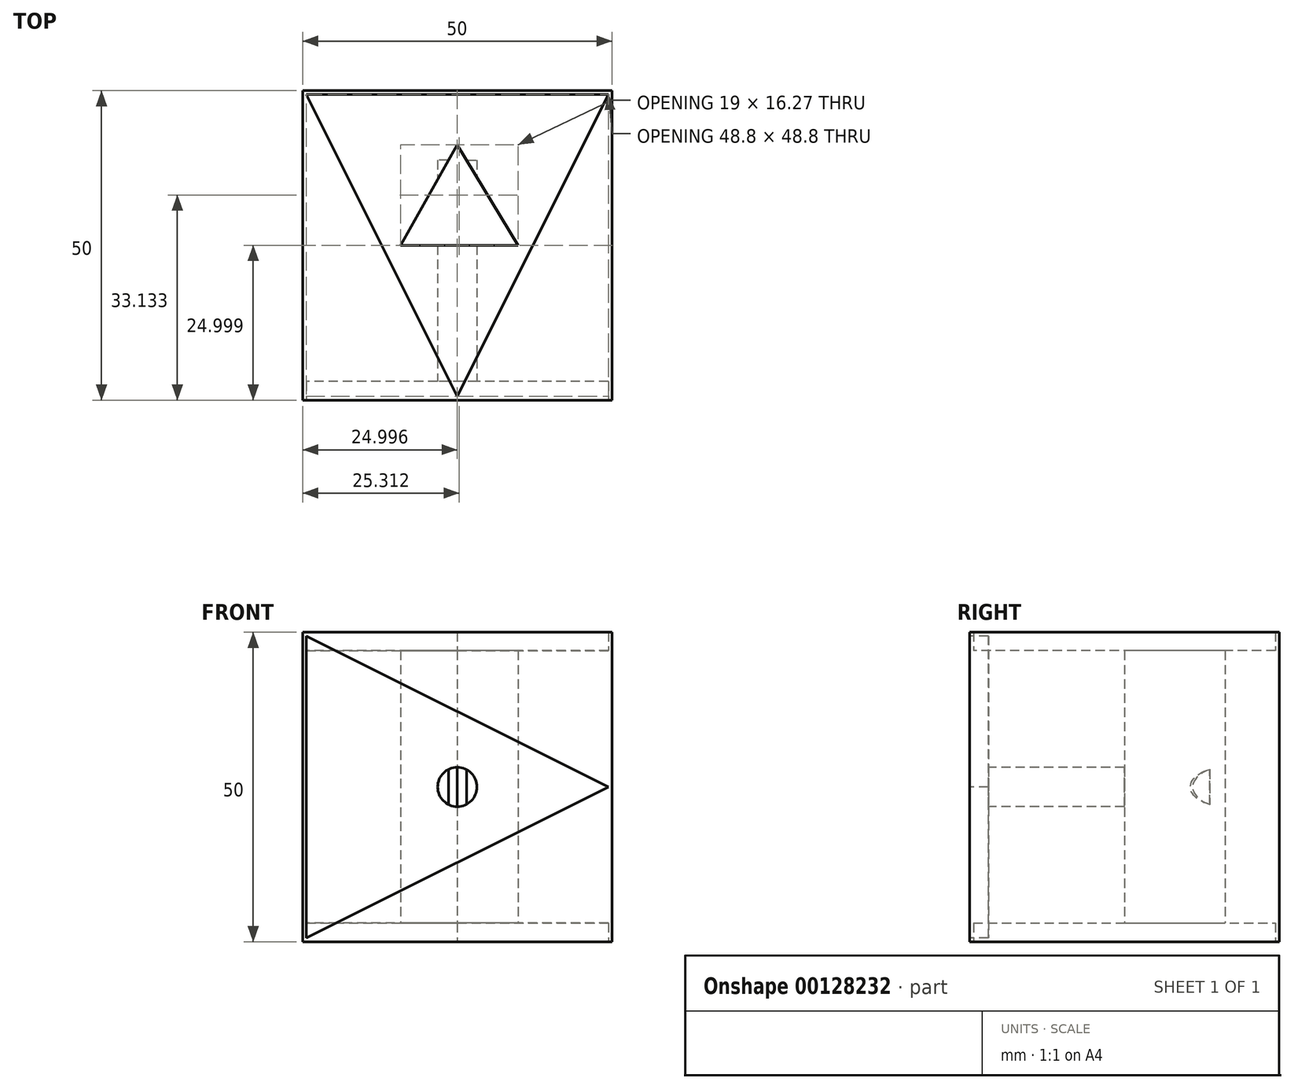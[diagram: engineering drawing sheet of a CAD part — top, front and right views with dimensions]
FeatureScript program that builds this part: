
annotation { "Feature Type Name" : "Feature", "Feature Type Description" : "" }
export const myFeature = defineFeature(function(context is Context, id is Id, definition is map)
    precondition{}
    {
        {
            var Q0;
            Q0=qCreatedBy(makeId("Top.planeOp"),FACE);
            var sketch = newSketch(context, id + "F0", { "sketchPlane" : qUnion([Q0])});
            skLineSegment(sketch, "E0", {"start": v(29.85, -17.75) * mm, "end": v(29.85, 32.25) * mm});
            skLineSegment(sketch, "E1", {"start": v(29.85, 32.25) * mm, "end": v(-20.15, 32.25) * mm});
            skLineSegment(sketch, "E2", {"start": v(-20.15, 32.25) * mm, "end": v(-20.15, -17.75) * mm});
            skLineSegment(sketch, "E3", {"start": v(29.85, -17.75) * mm, "end": v(-20.15, -17.75) * mm});
            skLineSegment(sketch, "E4", {"start": v(-19.56, 31.65) * mm, "end": v(4.85, -17.15) * mm});
            skLineSegment(sketch, "E5", {"start": v(4.85, -17.15) * mm, "end": v(29.25, 31.65) * mm});
            skLineSegment(sketch, "E6", {"start": v(29.25, 31.65) * mm, "end": v(-19.56, 31.65) * mm});
            skSolve(sketch);
        }
        {
            var Q0;
            Q0=makeQuery(id+"F0.imprint","IMPRINT",FACE,{"disambiguationData":[TD([[makeQuery(id+"F0.imprint","IMPRINT",EDGE,{"derivedFrom":sQuery(id+"F0.wireOp",EDGE,"E0")}),1.0]])]});
            extrude(context, id + "F1", {"entities" : qUnion([Q0]), "endBound" : BoundingType.SYMMETRIC, "depth" : 50 * mm});
        }
        {
            var Q0;
            Q0=makeQuery(id+"F0.imprint","IMPRINT",FACE,{"disambiguationData":[TD([[makeQuery(id+"F0.imprint","IMPRINT",EDGE,{"derivedFrom":sQuery(id+"F0.wireOp",EDGE,"E4")}),1.0]])]});
            extrude(context, id + "F2", {"entities" : qUnion([Q0]), "operationType" : NewBodyOperationType.ADD, "endBound" : BoundingType.SYMMETRIC, "depth" : 44 * mm});
        }
        {
            var Q0;
            Q0=makeQuery(id+"F2.opExtrude","CAP_FACE",FACE,{"disambiguationData":[OSD([sQuery(id+"F0.wireOp",EDGE,"E4"),sQuery(id+"F0.wireOp",EDGE,"E5"),sQuery(id+"F0.wireOp",EDGE,"E6")])],"isStart":true});
            var sketch = newSketch(context, id + "F3", { "sketchPlane" : qUnion([Q0])});
            skLineSegment(sketch, "E7.0.2", {"start": v(4.85, 17.15) * mm, "end": v(29.25, -31.65) * mm});
            skLineSegment(sketch, "E8", {"start": v(4.85, -23.52) * mm, "end": v(14.66, -7.25) * mm});
            skPoint(sketch, "E8.endSnap0", {"position": v(4.85, -7.25) * mm});
            skLineSegment(sketch, "E9", {"start": v(14.66, -7.25) * mm, "end": v(-4.34, -7.25) * mm});
            skLineSegment(sketch, "E10", {"start": v(-4.34, -7.25) * mm, "end": v(4.85, -23.52) * mm});
            skSolve(sketch);
        }
        {
            var Q0;
            Q0=makeQuery(id+"F3.imprint","IMPRINT",FACE,{"disambiguationData":[TD([[makeQuery(id+"F3.imprint","IMPRINT",EDGE,{"derivedFrom":sQuery(id+"F3.wireOp",EDGE,"E8")}),1.0]])]});
            extrude(context, id + "F4", {"entities" : qUnion([Q0]), "operationType" : NewBodyOperationType.REMOVE, "oppositeDirection" : true, "depth" : 48 * mm});
        }
        {
            var Q0;
            Q0=makeQuery(id+"F1.opExtrude","SWEPT_FACE",FACE,{"disambiguationData":[OSD([sQuery(id+"F0.wireOp",EDGE,"E3")])]});
            var sketch = newSketch(context, id + "F5", { "sketchPlane" : qUnion([Q0])});
            skCircle(sketch, "E11", {"center": v(4.85, 0) * mm, "radius": 3.18 * mm});
            skSolve(sketch);
        }
        {
            var Q0;
            Q0=makeQuery(id+"F5.imprint","IMPRINT",FACE,{"disambiguationData":[TD([[makeQuery(id+"F5.imprint","IMPRINT",EDGE,{"derivedFrom":sQuery(id+"F5.wireOp",EDGE,"E11")}),1.0]])]});
            extrude(context, id + "F6", {"entities" : qUnion([Q0]), "operationType" : NewBodyOperationType.REMOVE, "oppositeDirection" : true, "depth" : 38.77 * mm});
        }
        {
            var Q0;
            Q0=makeQuery(id+"F1.opExtrude","SWEPT_FACE",FACE,{"disambiguationData":[OSD([sQuery(id+"F0.wireOp",EDGE,"E3")])]});
            var sketch = newSketch(context, id + "F7", { "sketchPlane" : qUnion([Q0])});
            skLineSegment(sketch, "E12", {"start": v(-19.56, 24.4) * mm, "end": v(-19.56, -24.4) * mm});
            skLineSegment(sketch, "E13", {"start": v(-19.56, -24.4) * mm, "end": v(29.25, 0) * mm});
            skLineSegment(sketch, "E14", {"start": v(29.25, 0) * mm, "end": v(-19.56, 24.4) * mm});
            skSolve(sketch);
        }
        {
            var Q0;
            Q0=makeQuery(id+"F7.imprint","IMPRINT",FACE,{"disambiguationData":[TD([[makeQuery(id+"F7.imprint","IMPRINT",EDGE,{"derivedFrom":sQuery(id+"F7.wireOp",EDGE,"E12")}),1.0]])]});
            extrude(context, id + "F8", {"entities" : qUnion([Q0]), "operationType" : NewBodyOperationType.REMOVE, "oppositeDirection" : true, "depth" : 3 * mm});
        }
    });
